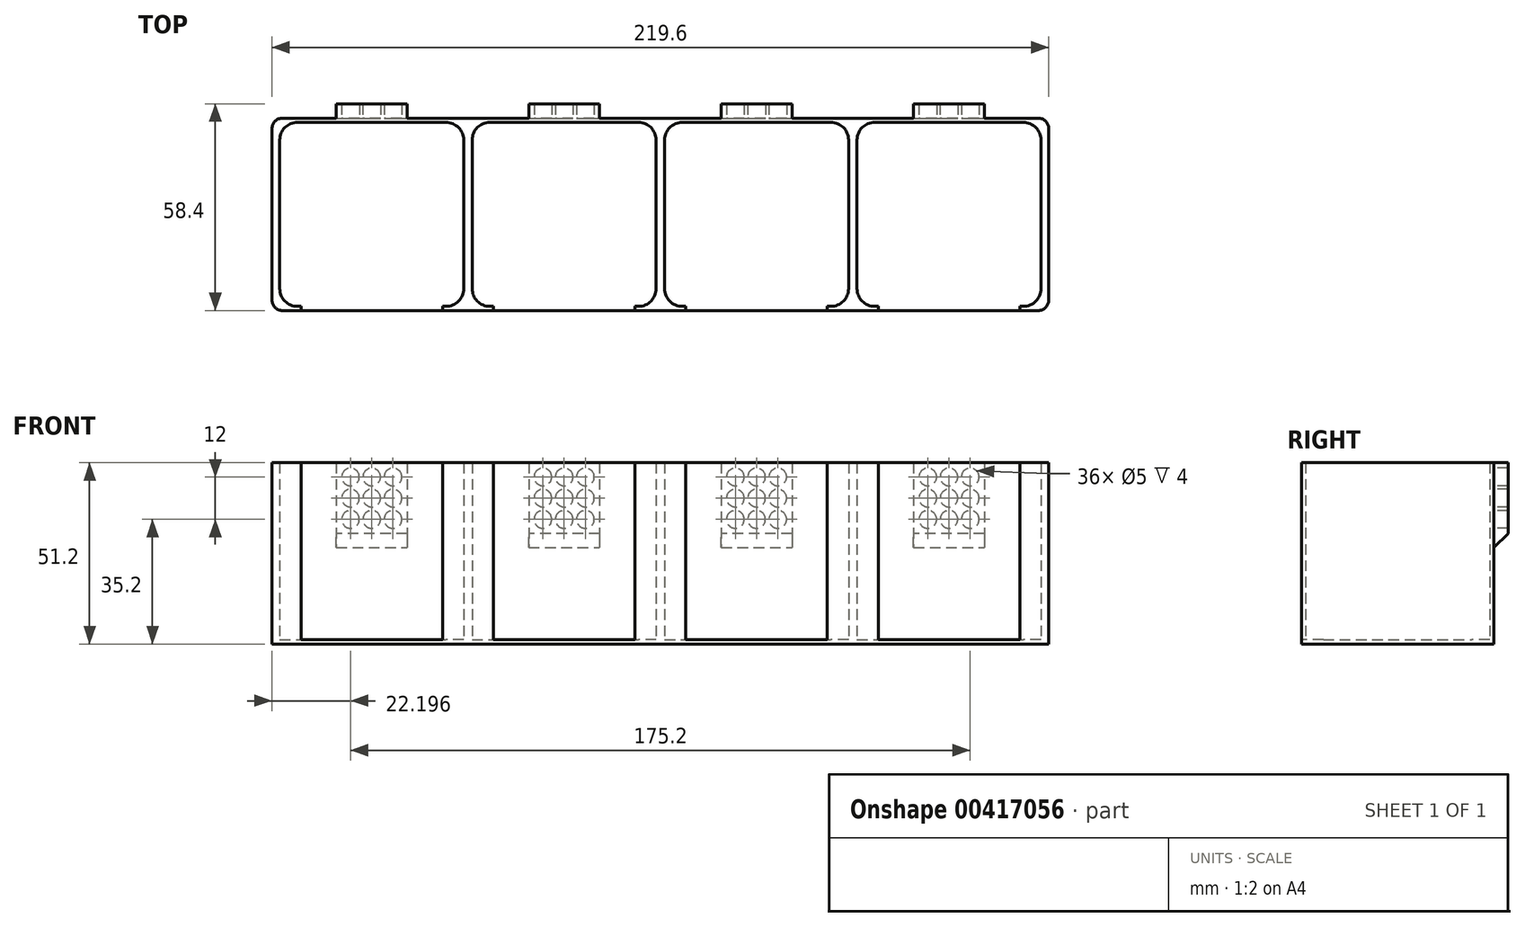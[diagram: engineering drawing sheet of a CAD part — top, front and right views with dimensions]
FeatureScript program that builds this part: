
annotation { "Feature Type Name" : "Feature", "Feature Type Description" : "" }
export const myFeature = defineFeature(function(context is Context, id is Id, definition is map)
    precondition{}
    {
        {
            var Q0;
            Q0=qCreatedBy(makeId("Top.planeOp"),FACE);
            var sketch = newSketch(context, id + "F0", { "sketchPlane" : qUnion([Q0])});
            skLineSegment(sketch, "E0.bottom", {"start": v(-53.6, -9.68) * mm, "end": v(-52.6, -9.68) * mm});
            skLineSegment(sketch, "E0.top", {"start": v(-53.6, 42.32) * mm, "end": v(-11.6, 42.32) * mm});
            skLineSegment(sketch, "E0.left", {"start": v(-58.6, -4.68) * mm, "end": v(-58.6, 37.32) * mm});
            skLineSegment(sketch, "E0.right", {"start": v(-6.6, -4.68) * mm, "end": v(-6.6, 37.32) * mm});
            skCircle(sketch, "E1", {"center": v(-32.6, -9.68) * mm, "radius": 20 * mm, "construction": true});
            skLineSegment(sketch, "E2.trimOffspring", {"start": v(-12.6, -9.68) * mm, "end": v(-11.6, -9.68) * mm});
            skLineSegment(sketch, "E3.0", {"start": v(-12.6, -10.88) * mm, "end": v(-5.4, -10.88) * mm});
            skLineSegment(sketch, "E3.1", {"start": v(-59.8, -10.88) * mm, "end": v(-52.56, -10.88) * mm});
            skLineSegment(sketch, "E3.2", {"start": v(-59.8, -10.88) * mm, "end": v(-59.8, 43.52) * mm});
            skLineSegment(sketch, "E3.3", {"start": v(-59.8, 43.52) * mm, "end": v(-5.4, 43.52) * mm});
            skLineSegment(sketch, "E3.4", {"start": v(-5.4, -10.88) * mm, "end": v(-5.4, 43.52) * mm});
            skLineSegment(sketch, "E4", {"start": v(-52.6, -9.68) * mm, "end": v(-52.6, -10.88) * mm});
            skLineSegment(sketch, "E5", {"start": v(-12.6, -9.68) * mm, "end": v(-12.6, -10.88) * mm});
            skPoint(sketch, "E6.visualSharp", {"position": v(-58.6, 42.32) * mm});
            skArc(sketch, "E6.filletArc", {"start": v(-53.6, 42.32) * mm, "mid": v(-57.13, 40.85) * mm, "end": v(-58.6, 37.32) * mm});
            skPoint(sketch, "E7.visualSharp", {"position": v(-6.6, 42.32) * mm});
            skArc(sketch, "E7.filletArc", {"start": v(-6.6, 37.32) * mm, "mid": v(-8.06, 40.85) * mm, "end": v(-11.6, 42.32) * mm});
            skPoint(sketch, "E8.visualSharp", {"position": v(-58.6, -9.68) * mm});
            skArc(sketch, "E8.filletArc", {"start": v(-58.6, -4.68) * mm, "mid": v(-57.13, -8.22) * mm, "end": v(-53.6, -9.68) * mm});
            skPoint(sketch, "E9.visualSharp", {"position": v(-6.6, -9.68) * mm});
            skArc(sketch, "E9.filletArc", {"start": v(-11.6, -9.68) * mm, "mid": v(-8.06, -8.22) * mm, "end": v(-6.6, -4.68) * mm});
            skPoint(sketch, "E10.1.0.0", {"position": v(-4.2, -9.68) * mm});
            skPoint(sketch, "E10.1.0.1", {"position": v(47.8, 42.32) * mm});
            skPoint(sketch, "E10.1.0.2", {"position": v(-4.2, 42.32) * mm});
            skPoint(sketch, "E10.1.0.3", {"position": v(47.8, -9.68) * mm});
            skLineSegment(sketch, "E10.1.0.4", {"start": v(49, -10.88) * mm, "end": v(49, 43.52) * mm});
            skLineSegment(sketch, "E10.1.0.5", {"start": v(-5.4, 43.52) * mm, "end": v(49, 43.52) * mm});
            skCircle(sketch, "E10.1.0.7", {"center": v(21.8, -9.68) * mm, "radius": 20 * mm, "construction": true});
            skLineSegment(sketch, "E10.1.0.8", {"start": v(-4.2, -4.68) * mm, "end": v(-4.2, 37.32) * mm});
            skLineSegment(sketch, "E10.1.0.9", {"start": v(47.8, -4.68) * mm, "end": v(47.8, 37.32) * mm});
            skLineSegment(sketch, "E10.1.0.10", {"start": v(0.8, 42.32) * mm, "end": v(42.8, 42.32) * mm});
            skArc(sketch, "E10.1.0.11", {"start": v(-4.2, -4.68) * mm, "mid": v(-2.73, -8.22) * mm, "end": v(0.8, -9.68) * mm});
            skArc(sketch, "E10.1.0.12", {"start": v(47.8, 37.32) * mm, "mid": v(46.34, 40.85) * mm, "end": v(42.8, 42.32) * mm});
            skArc(sketch, "E10.1.0.13", {"start": v(0.8, 42.32) * mm, "mid": v(-2.73, 40.85) * mm, "end": v(-4.2, 37.32) * mm});
            skArc(sketch, "E10.1.0.14", {"start": v(42.8, -9.68) * mm, "mid": v(46.34, -8.22) * mm, "end": v(47.8, -4.68) * mm});
            skLineSegment(sketch, "E10.1.0.15", {"start": v(-5.4, -10.88) * mm, "end": v(1.84, -10.88) * mm});
            skLineSegment(sketch, "E10.1.0.16", {"start": v(41.8, -10.88) * mm, "end": v(49, -10.88) * mm});
            skLineSegment(sketch, "E10.1.0.17", {"start": v(0.8, -9.68) * mm, "end": v(1.8, -9.68) * mm});
            skLineSegment(sketch, "E10.1.0.18", {"start": v(41.8, -9.68) * mm, "end": v(41.8, -10.88) * mm});
            skLineSegment(sketch, "E10.1.0.19", {"start": v(1.8, -9.68) * mm, "end": v(1.8, -10.88) * mm});
            skLineSegment(sketch, "E10.1.0.20", {"start": v(41.8, -9.68) * mm, "end": v(42.8, -9.68) * mm});
            skPoint(sketch, "E10.2.0.0", {"position": v(50.2, -9.68) * mm});
            skPoint(sketch, "E10.2.0.1", {"position": v(102.2, 42.32) * mm});
            skPoint(sketch, "E10.2.0.2", {"position": v(50.2, 42.32) * mm});
            skPoint(sketch, "E10.2.0.3", {"position": v(102.2, -9.68) * mm});
            skLineSegment(sketch, "E10.2.0.4", {"start": v(103.4, -10.88) * mm, "end": v(103.4, 43.52) * mm});
            skLineSegment(sketch, "E10.2.0.5", {"start": v(49, 43.52) * mm, "end": v(103.4, 43.52) * mm});
            skLineSegment(sketch, "E10.2.0.6", {"start": v(49, -10.88) * mm, "end": v(49, 43.52) * mm});
            skCircle(sketch, "E10.2.0.7", {"center": v(76.2, -9.68) * mm, "radius": 20 * mm, "construction": true});
            skLineSegment(sketch, "E10.2.0.8", {"start": v(50.2, -4.68) * mm, "end": v(50.2, 37.32) * mm});
            skLineSegment(sketch, "E10.2.0.9", {"start": v(102.2, -4.68) * mm, "end": v(102.2, 37.32) * mm});
            skLineSegment(sketch, "E10.2.0.10", {"start": v(55.2, 42.32) * mm, "end": v(97.2, 42.32) * mm});
            skArc(sketch, "E10.2.0.11", {"start": v(50.2, -4.68) * mm, "mid": v(51.67, -8.22) * mm, "end": v(55.2, -9.68) * mm});
            skArc(sketch, "E10.2.0.12", {"start": v(102.2, 37.32) * mm, "mid": v(100.74, 40.85) * mm, "end": v(97.2, 42.32) * mm});
            skArc(sketch, "E10.2.0.13", {"start": v(55.2, 42.32) * mm, "mid": v(51.67, 40.85) * mm, "end": v(50.2, 37.32) * mm});
            skArc(sketch, "E10.2.0.14", {"start": v(97.2, -9.68) * mm, "mid": v(100.74, -8.22) * mm, "end": v(102.2, -4.68) * mm});
            skLineSegment(sketch, "E10.2.0.15", {"start": v(49, -10.88) * mm, "end": v(56.24, -10.88) * mm});
            skLineSegment(sketch, "E10.2.0.16", {"start": v(96.2, -10.88) * mm, "end": v(103.4, -10.88) * mm});
            skLineSegment(sketch, "E10.2.0.17", {"start": v(55.2, -9.68) * mm, "end": v(56.2, -9.68) * mm});
            skLineSegment(sketch, "E10.2.0.18", {"start": v(96.2, -9.68) * mm, "end": v(96.2, -10.88) * mm});
            skLineSegment(sketch, "E10.2.0.19", {"start": v(56.2, -9.68) * mm, "end": v(56.2, -10.88) * mm});
            skLineSegment(sketch, "E10.2.0.20", {"start": v(96.2, -9.68) * mm, "end": v(97.2, -9.68) * mm});
            skPoint(sketch, "E10.3.0.0", {"position": v(104.6, -9.68) * mm});
            skPoint(sketch, "E10.3.0.1", {"position": v(156.6, 42.32) * mm});
            skPoint(sketch, "E10.3.0.2", {"position": v(104.6, 42.32) * mm});
            skPoint(sketch, "E10.3.0.3", {"position": v(156.6, -9.68) * mm});
            skLineSegment(sketch, "E10.3.0.4", {"start": v(157.8, -10.88) * mm, "end": v(157.8, 43.52) * mm});
            skLineSegment(sketch, "E10.3.0.5", {"start": v(103.4, 43.52) * mm, "end": v(157.8, 43.52) * mm});
            skLineSegment(sketch, "E10.3.0.6", {"start": v(103.4, -10.88) * mm, "end": v(103.4, 43.52) * mm});
            skCircle(sketch, "E10.3.0.7", {"center": v(130.6, -9.68) * mm, "radius": 20 * mm, "construction": true});
            skLineSegment(sketch, "E10.3.0.8", {"start": v(104.6, -4.68) * mm, "end": v(104.6, 37.32) * mm});
            skLineSegment(sketch, "E10.3.0.9", {"start": v(156.6, -4.68) * mm, "end": v(156.6, 37.32) * mm});
            skLineSegment(sketch, "E10.3.0.10", {"start": v(109.6, 42.32) * mm, "end": v(151.6, 42.32) * mm});
            skArc(sketch, "E10.3.0.11", {"start": v(104.6, -4.68) * mm, "mid": v(106.07, -8.22) * mm, "end": v(109.6, -9.68) * mm});
            skArc(sketch, "E10.3.0.12", {"start": v(156.6, 37.32) * mm, "mid": v(155.14, 40.85) * mm, "end": v(151.6, 42.32) * mm});
            skArc(sketch, "E10.3.0.13", {"start": v(109.6, 42.32) * mm, "mid": v(106.07, 40.85) * mm, "end": v(104.6, 37.32) * mm});
            skArc(sketch, "E10.3.0.14", {"start": v(151.6, -9.68) * mm, "mid": v(155.14, -8.22) * mm, "end": v(156.6, -4.68) * mm});
            skLineSegment(sketch, "E10.3.0.15", {"start": v(103.4, -10.88) * mm, "end": v(110.64, -10.88) * mm});
            skLineSegment(sketch, "E10.3.0.16", {"start": v(150.6, -10.88) * mm, "end": v(157.8, -10.88) * mm});
            skLineSegment(sketch, "E10.3.0.17", {"start": v(109.6, -9.68) * mm, "end": v(110.6, -9.68) * mm});
            skLineSegment(sketch, "E10.3.0.18", {"start": v(150.6, -9.68) * mm, "end": v(150.6, -10.88) * mm});
            skLineSegment(sketch, "E10.3.0.19", {"start": v(110.6, -9.68) * mm, "end": v(110.6, -10.88) * mm});
            skLineSegment(sketch, "E10.3.0.20", {"start": v(150.6, -9.68) * mm, "end": v(151.6, -9.68) * mm});
            skLineSegment(sketch, "E10.direction1", {"start": v(-59.8, -10.88) * mm, "end": v(-5.4, -10.88) * mm, "construction": true});
            skLineSegment(sketch, "E11.bottom", {"start": v(-59.8, 43.52) * mm, "end": v(-60.8, 43.52) * mm});
            skLineSegment(sketch, "E11.top", {"start": v(-59.8, -10.88) * mm, "end": v(-60.8, -10.88) * mm});
            skLineSegment(sketch, "E11.left", {"start": v(-59.8, 43.52) * mm, "end": v(-59.8, -10.88) * mm});
            skLineSegment(sketch, "E11.right", {"start": v(-60.8, 43.52) * mm, "end": v(-60.8, -10.88) * mm});
            skLineSegment(sketch, "E12.bottom", {"start": v(157.8, 43.52) * mm, "end": v(158.8, 43.52) * mm});
            skLineSegment(sketch, "E12.top", {"start": v(157.8, -10.88) * mm, "end": v(158.8, -10.88) * mm});
            skLineSegment(sketch, "E12.left", {"start": v(157.8, 43.52) * mm, "end": v(157.8, -10.88) * mm});
            skLineSegment(sketch, "E12.right", {"start": v(158.8, 43.52) * mm, "end": v(158.8, -10.88) * mm});
            skSolve(sketch);
        }
        {
            var Q0;
            Q0 = qSketchRegion(id + "F0", true);
            extrude(context, id + "F1", {"entities" : qUnion([Q0]), "depth" : 50 * mm});
        }
        {
            var Q0;
            Q0=makeQuery(id+"F1.opExtrude","CAP_FACE",FACE,{"disambiguationData":[OSD([sQuery(id+"F0.wireOp",EDGE,"E0.bottom"),sQuery(id+"F0.wireOp",EDGE,"E0.top"),sQuery(id+"F0.wireOp",EDGE,"E0.left"),sQuery(id+"F0.wireOp",EDGE,"E0.right"),sQuery(id+"F0.wireOp",EDGE,"E2.trimOffspring"),sQuery(id+"F0.wireOp",EDGE,"E3.0"),sQuery(id+"F0.wireOp",EDGE,"E3.1"),sQuery(id+"F0.wireOp",EDGE,"E3.2"),sQuery(id+"F0.wireOp",EDGE,"E3.3"),sQuery(id+"F0.wireOp",EDGE,"E4"),sQuery(id+"F0.wireOp",EDGE,"E5"),sQuery(id+"F0.wireOp",EDGE,"E6.filletArc"),sQuery(id+"F0.wireOp",EDGE,"E7.filletArc"),sQuery(id+"F0.wireOp",EDGE,"E8.filletArc"),sQuery(id+"F0.wireOp",EDGE,"E9.filletArc"),sQuery(id+"F0.wireOp",EDGE,"E10.1.0.5"),sQuery(id+"F0.wireOp",EDGE,"E10.1.0.8"),sQuery(id+"F0.wireOp",EDGE,"E10.1.0.9"),sQuery(id+"F0.wireOp",EDGE,"E10.1.0.10"),sQuery(id+"F0.wireOp",EDGE,"E10.1.0.11"),sQuery(id+"F0.wireOp",EDGE,"E10.1.0.12"),sQuery(id+"F0.wireOp",EDGE,"E10.1.0.13"),sQuery(id+"F0.wireOp",EDGE,"E10.1.0.14"),sQuery(id+"F0.wireOp",EDGE,"E10.1.0.15"),sQuery(id+"F0.wireOp",EDGE,"E10.1.0.16"),sQuery(id+"F0.wireOp",EDGE,"E10.1.0.17"),sQuery(id+"F0.wireOp",EDGE,"E10.1.0.18"),sQuery(id+"F0.wireOp",EDGE,"E10.1.0.19"),sQuery(id+"F0.wireOp",EDGE,"E10.1.0.20"),sQuery(id+"F0.wireOp",EDGE,"E10.2.0.5"),sQuery(id+"F0.wireOp",EDGE,"E10.2.0.8"),sQuery(id+"F0.wireOp",EDGE,"E10.2.0.9"),sQuery(id+"F0.wireOp",EDGE,"E10.2.0.10"),sQuery(id+"F0.wireOp",EDGE,"E10.2.0.11"),sQuery(id+"F0.wireOp",EDGE,"E10.2.0.12"),sQuery(id+"F0.wireOp",EDGE,"E10.2.0.13"),sQuery(id+"F0.wireOp",EDGE,"E10.2.0.14"),sQuery(id+"F0.wireOp",EDGE,"E10.2.0.15"),sQuery(id+"F0.wireOp",EDGE,"E10.2.0.16"),sQuery(id+"F0.wireOp",EDGE,"E10.2.0.17"),sQuery(id+"F0.wireOp",EDGE,"E10.2.0.18"),sQuery(id+"F0.wireOp",EDGE,"E10.2.0.19"),sQuery(id+"F0.wireOp",EDGE,"E10.2.0.20"),sQuery(id+"F0.wireOp",EDGE,"E10.3.0.5"),sQuery(id+"F0.wireOp",EDGE,"E10.3.0.8"),sQuery(id+"F0.wireOp",EDGE,"E10.3.0.9"),sQuery(id+"F0.wireOp",EDGE,"E10.3.0.10"),sQuery(id+"F0.wireOp",EDGE,"E10.3.0.11"),sQuery(id+"F0.wireOp",EDGE,"E10.3.0.12"),sQuery(id+"F0.wireOp",EDGE,"E10.3.0.13"),sQuery(id+"F0.wireOp",EDGE,"E10.3.0.14"),sQuery(id+"F0.wireOp",EDGE,"E10.3.0.15"),sQuery(id+"F0.wireOp",EDGE,"E10.3.0.16"),sQuery(id+"F0.wireOp",EDGE,"E10.3.0.17"),sQuery(id+"F0.wireOp",EDGE,"E10.3.0.18"),sQuery(id+"F0.wireOp",EDGE,"E10.3.0.19"),sQuery(id+"F0.wireOp",EDGE,"E10.3.0.20"),sQuery(id+"F0.wireOp",EDGE,"E10.4.0.4"),sQuery(id+"F0.wireOp",EDGE,"E10.4.0.5"),sQuery(id+"F0.wireOp",EDGE,"E10.4.0.8"),sQuery(id+"F0.wireOp",EDGE,"E10.4.0.9"),sQuery(id+"F0.wireOp",EDGE,"E10.4.0.10"),sQuery(id+"F0.wireOp",EDGE,"E10.4.0.11"),sQuery(id+"F0.wireOp",EDGE,"E10.4.0.12"),sQuery(id+"F0.wireOp",EDGE,"E10.4.0.13"),sQuery(id+"F0.wireOp",EDGE,"E10.4.0.14"),sQuery(id+"F0.wireOp",EDGE,"E10.4.0.15"),sQuery(id+"F0.wireOp",EDGE,"E10.4.0.16"),sQuery(id+"F0.wireOp",EDGE,"E10.4.0.17"),sQuery(id+"F0.wireOp",EDGE,"E10.4.0.18"),sQuery(id+"F0.wireOp",EDGE,"E10.4.0.19"),sQuery(id+"F0.wireOp",EDGE,"E10.4.0.20")])],"isStart":true});
            var sketch = newSketch(context, id + "F2", { "sketchPlane" : qUnion([Q0])});
            skLineSegment(sketch, "E13.bottom", {"start": v(-60.8, 10.88) * mm, "end": v(158.8, 10.88) * mm});
            skLineSegment(sketch, "E13.top", {"start": v(-60.8, -43.52) * mm, "end": v(158.8, -43.52) * mm});
            skLineSegment(sketch, "E13.left", {"start": v(-60.8, 10.88) * mm, "end": v(-60.8, -43.52) * mm});
            skLineSegment(sketch, "E13.right", {"start": v(158.8, 10.88) * mm, "end": v(158.8, -43.52) * mm});
            skSolve(sketch);
        }
        {
            var Q0;
            Q0 = qSketchRegion(id + "F2", true);
            extrude(context, id + "F3", {"entities" : qUnion([Q0]), "operationType" : NewBodyOperationType.ADD, "depth" : 1.2 * mm});
        }
        {
            var Q0;
            Q0=makeQuery(id+"F1.opExtrude","SWEPT_FACE",FACE,{"disambiguationData":[OSD([sQuery(id+"F0.wireOp",EDGE,"E0.top")])]});
            var sketch = newSketch(context, id + "F4", { "sketchPlane" : qUnion([Q0])});
            skLineSegment(sketch, "E14.bottom", {"start": v(-22.6, 50) * mm, "end": v(-42.6, 50) * mm});
            skLineSegment(sketch, "E14.top", {"start": v(-22.6, 30) * mm, "end": v(-42.6, 30) * mm});
            skLineSegment(sketch, "E14.left", {"start": v(-22.6, 50) * mm, "end": v(-22.6, 30) * mm});
            skLineSegment(sketch, "E14.right", {"start": v(-42.6, 50) * mm, "end": v(-42.6, 30) * mm});
            skPoint(sketch, "E14.middle", {"position": v(-32.6, 40) * mm});
            skPoint(sketch, "E14.middle.positionSnap0", {"position": v(-32.6, 50) * mm});
            skPoint(sketch, "E14.centerSnap0", {"position": v(-32.6, 50) * mm});
            skCircle(sketch, "E15", {"center": v(-38.6, 34) * mm, "radius": 2.5 * mm});
            skCircle(sketch, "E16.0.1.0", {"center": v(-38.6, 40) * mm, "radius": 2.5 * mm});
            skCircle(sketch, "E16.0.2.0", {"center": v(-38.6, 46) * mm, "radius": 2.5 * mm});
            skCircle(sketch, "E16.1.0.0", {"center": v(-32.6, 34) * mm, "radius": 2.5 * mm});
            skCircle(sketch, "E16.1.1.0", {"center": v(-32.6, 40) * mm, "radius": 2.5 * mm});
            skCircle(sketch, "E16.1.2.0", {"center": v(-32.6, 46) * mm, "radius": 2.5 * mm});
            skCircle(sketch, "E16.2.0.0", {"center": v(-26.6, 34) * mm, "radius": 2.5 * mm});
            skCircle(sketch, "E16.2.1.0", {"center": v(-26.6, 40) * mm, "radius": 2.5 * mm});
            skCircle(sketch, "E16.2.2.0", {"center": v(-26.6, 46) * mm, "radius": 2.5 * mm});
            skLineSegment(sketch, "E16.direction1", {"start": v(-38.6, 34) * mm, "end": v(-32.6, 34) * mm, "construction": true});
            skLineSegment(sketch, "E16.direction2", {"start": v(-38.6, 34) * mm, "end": v(-38.6, 40) * mm, "construction": true});
            skPoint(sketch, "E17.1.0.0", {"position": v(21.8, 50) * mm});
            skCircle(sketch, "E17.1.0.1", {"center": v(27.8, 40) * mm, "radius": 2.5 * mm});
            skCircle(sketch, "E17.1.0.2", {"center": v(15.8, 34) * mm, "radius": 2.5 * mm});
            skCircle(sketch, "E17.1.0.3", {"center": v(21.8, 40) * mm, "radius": 2.5 * mm});
            skCircle(sketch, "E17.1.0.4", {"center": v(15.8, 40) * mm, "radius": 2.5 * mm});
            skCircle(sketch, "E17.1.0.5", {"center": v(27.8, 34) * mm, "radius": 2.5 * mm});
            skPoint(sketch, "E17.1.0.6", {"position": v(21.8, 40) * mm});
            skLineSegment(sketch, "E17.1.0.7", {"start": v(31.8, 30) * mm, "end": v(11.8, 30) * mm});
            skLineSegment(sketch, "E17.1.0.8", {"start": v(31.8, 50) * mm, "end": v(11.8, 50) * mm});
            skLineSegment(sketch, "E17.1.0.9", {"start": v(11.8, 50) * mm, "end": v(11.8, 30) * mm});
            skLineSegment(sketch, "E17.1.0.10", {"start": v(31.8, 50) * mm, "end": v(31.8, 30) * mm});
            skCircle(sketch, "E17.1.0.11", {"center": v(21.8, 34) * mm, "radius": 2.5 * mm});
            skCircle(sketch, "E17.1.0.12", {"center": v(21.8, 46) * mm, "radius": 2.5 * mm});
            skCircle(sketch, "E17.1.0.13", {"center": v(15.8, 46) * mm, "radius": 2.5 * mm});
            skCircle(sketch, "E17.1.0.14", {"center": v(27.8, 46) * mm, "radius": 2.5 * mm});
            skLineSegment(sketch, "E17.1.0.15", {"start": v(15.8, 34) * mm, "end": v(15.8, 40) * mm, "construction": true});
            skLineSegment(sketch, "E17.1.0.16", {"start": v(15.8, 34) * mm, "end": v(21.8, 34) * mm, "construction": true});
            skPoint(sketch, "E17.1.0.17", {"position": v(21.8, 50) * mm});
            skPoint(sketch, "E17.2.0.0", {"position": v(76.2, 50) * mm});
            skCircle(sketch, "E17.2.0.1", {"center": v(82.2, 40) * mm, "radius": 2.5 * mm});
            skCircle(sketch, "E17.2.0.2", {"center": v(70.2, 34) * mm, "radius": 2.5 * mm});
            skCircle(sketch, "E17.2.0.3", {"center": v(76.2, 40) * mm, "radius": 2.5 * mm});
            skCircle(sketch, "E17.2.0.4", {"center": v(70.2, 40) * mm, "radius": 2.5 * mm});
            skCircle(sketch, "E17.2.0.5", {"center": v(82.2, 34) * mm, "radius": 2.5 * mm});
            skPoint(sketch, "E17.2.0.6", {"position": v(76.2, 40) * mm});
            skLineSegment(sketch, "E17.2.0.7", {"start": v(86.2, 30) * mm, "end": v(66.2, 30) * mm});
            skLineSegment(sketch, "E17.2.0.8", {"start": v(86.2, 50) * mm, "end": v(66.2, 50) * mm});
            skLineSegment(sketch, "E17.2.0.9", {"start": v(66.2, 50) * mm, "end": v(66.2, 30) * mm});
            skLineSegment(sketch, "E17.2.0.10", {"start": v(86.2, 50) * mm, "end": v(86.2, 30) * mm});
            skCircle(sketch, "E17.2.0.11", {"center": v(76.2, 34) * mm, "radius": 2.5 * mm});
            skCircle(sketch, "E17.2.0.12", {"center": v(76.2, 46) * mm, "radius": 2.5 * mm});
            skCircle(sketch, "E17.2.0.13", {"center": v(70.2, 46) * mm, "radius": 2.5 * mm});
            skCircle(sketch, "E17.2.0.14", {"center": v(82.2, 46) * mm, "radius": 2.5 * mm});
            skLineSegment(sketch, "E17.2.0.15", {"start": v(70.2, 34) * mm, "end": v(70.2, 40) * mm, "construction": true});
            skLineSegment(sketch, "E17.2.0.16", {"start": v(70.2, 34) * mm, "end": v(76.2, 34) * mm, "construction": true});
            skPoint(sketch, "E17.2.0.17", {"position": v(76.2, 50) * mm});
            skPoint(sketch, "E17.3.0.0", {"position": v(130.6, 50) * mm});
            skCircle(sketch, "E17.3.0.1", {"center": v(136.6, 40) * mm, "radius": 2.5 * mm});
            skCircle(sketch, "E17.3.0.2", {"center": v(124.6, 34) * mm, "radius": 2.5 * mm});
            skCircle(sketch, "E17.3.0.3", {"center": v(130.6, 40) * mm, "radius": 2.5 * mm});
            skCircle(sketch, "E17.3.0.4", {"center": v(124.6, 40) * mm, "radius": 2.5 * mm});
            skCircle(sketch, "E17.3.0.5", {"center": v(136.6, 34) * mm, "radius": 2.5 * mm});
            skPoint(sketch, "E17.3.0.6", {"position": v(130.6, 40) * mm});
            skLineSegment(sketch, "E17.3.0.7", {"start": v(140.6, 30) * mm, "end": v(120.6, 30) * mm});
            skLineSegment(sketch, "E17.3.0.8", {"start": v(140.6, 50) * mm, "end": v(120.6, 50) * mm});
            skLineSegment(sketch, "E17.3.0.9", {"start": v(120.6, 50) * mm, "end": v(120.6, 30) * mm});
            skLineSegment(sketch, "E17.3.0.10", {"start": v(140.6, 50) * mm, "end": v(140.6, 30) * mm});
            skCircle(sketch, "E17.3.0.11", {"center": v(130.6, 34) * mm, "radius": 2.5 * mm});
            skCircle(sketch, "E17.3.0.12", {"center": v(130.6, 46) * mm, "radius": 2.5 * mm});
            skCircle(sketch, "E17.3.0.13", {"center": v(124.6, 46) * mm, "radius": 2.5 * mm});
            skCircle(sketch, "E17.3.0.14", {"center": v(136.6, 46) * mm, "radius": 2.5 * mm});
            skLineSegment(sketch, "E17.3.0.15", {"start": v(124.6, 34) * mm, "end": v(124.6, 40) * mm, "construction": true});
            skLineSegment(sketch, "E17.3.0.16", {"start": v(124.6, 34) * mm, "end": v(130.6, 34) * mm, "construction": true});
            skPoint(sketch, "E17.3.0.17", {"position": v(130.6, 50) * mm});
            skLineSegment(sketch, "E17.direction1", {"start": v(-42.6, 30) * mm, "end": v(11.8, 30) * mm, "construction": true});
            skSolve(sketch);
        }
        {
            var Q0;
            Q0 = qSketchRegion(id + "F4", true);
            extrude(context, id + "F5", {"entities" : qUnion([Q0]), "operationType" : NewBodyOperationType.ADD, "oppositeDirection" : true, "depth" : 5.2 * mm});
        }
        {
            var Q0;
            Q0=makeQuery(id+"F3.boolean.opBoolean","MERGE",EDGE,{"derivedFrom":[makeQuery(id+"F1.opExtrude","SWEPT_EDGE",EDGE,{"disambiguationData":[OSD([sQuery(id+"F0.wireOp",EDGE,"E11.top"),sQuery(id+"F0.wireOp",EDGE,"E11.right")])]}),makeQuery(id+"F3.opExtrude","SWEPT_EDGE",EDGE,{"disambiguationData":[OSD([sQuery(id+"F2.wireOp",EDGE,"E13.bottom"),sQuery(id+"F2.wireOp",EDGE,"E13.left")])]})]});
            var Q1;
            Q1=makeQuery(id+"F3.boolean.opBoolean","MERGE",EDGE,{"derivedFrom":[makeQuery(id+"F1.opExtrude","SWEPT_EDGE",EDGE,{"disambiguationData":[OSD([sQuery(id+"F0.wireOp",EDGE,"E12.top"),sQuery(id+"F0.wireOp",EDGE,"E12.right")])]}),makeQuery(id+"F3.opExtrude","SWEPT_EDGE",EDGE,{"disambiguationData":[OSD([sQuery(id+"F2.wireOp",EDGE,"E13.bottom"),sQuery(id+"F2.wireOp",EDGE,"E13.right")])]})]});
            var Q2;
            Q2=makeQuery(id+"F3.boolean.opBoolean","MERGE",EDGE,{"derivedFrom":[makeQuery(id+"F1.opExtrude","SWEPT_EDGE",EDGE,{"disambiguationData":[OSD([sQuery(id+"F0.wireOp",EDGE,"E11.bottom"),sQuery(id+"F0.wireOp",EDGE,"E11.right")])]}),makeQuery(id+"F3.opExtrude","SWEPT_EDGE",EDGE,{"disambiguationData":[OSD([sQuery(id+"F2.wireOp",EDGE,"E13.top"),sQuery(id+"F2.wireOp",EDGE,"E13.left")])]})]});
            var Q3;
            Q3=makeQuery(id+"F3.boolean.opBoolean","MERGE",EDGE,{"derivedFrom":[makeQuery(id+"F1.opExtrude","SWEPT_EDGE",EDGE,{"disambiguationData":[OSD([sQuery(id+"F0.wireOp",EDGE,"E12.bottom"),sQuery(id+"F0.wireOp",EDGE,"E12.right")])]}),makeQuery(id+"F3.opExtrude","SWEPT_EDGE",EDGE,{"disambiguationData":[OSD([sQuery(id+"F2.wireOp",EDGE,"E13.top"),sQuery(id+"F2.wireOp",EDGE,"E13.right")])]})]});
            fillet(context, id + "F6", {"entities" : qUnion([Q0, Q1, Q2, Q3]), "radius" : 3 * mm, "tangentPropagation" : true, "allowEdgeOverflow" : false});
        }
        {
            var Q0;
            Q0=makeQuery(id+"F5.boolean.opBoolean","INTERSECT",EDGE,{"derivedFrom":[makeQuery(id+"F3.boolean.opBoolean","MERGE",FACE,{"derivedFrom":[makeQuery(id+"F1.opExtrude","SWEPT_FACE",FACE,{"disambiguationData":[OSD([sQuery(id+"F0.wireOp",EDGE,"E3.3"),sQuery(id+"F0.wireOp",EDGE,"E10.1.0.5"),sQuery(id+"F0.wireOp",EDGE,"E10.2.0.5"),sQuery(id+"F0.wireOp",EDGE,"E10.3.0.5"),sQuery(id+"F0.wireOp",EDGE,"E11.bottom"),sQuery(id+"F0.wireOp",EDGE,"E12.bottom")])]}),makeQuery(id+"F3.opExtrude","SWEPT_FACE",FACE,{"disambiguationData":[OSD([sQuery(id+"F2.wireOp",EDGE,"E13.top")])]})]}),makeQuery(id+"F5.opExtrude","SWEPT_FACE",FACE,{"disambiguationData":[OSD([sQuery(id+"F4.wireOp",EDGE,"E17.3.0.7")])]})]});
            var Q1;
            Q1=makeQuery(id+"F5.boolean.opBoolean","INTERSECT",EDGE,{"derivedFrom":[makeQuery(id+"F3.boolean.opBoolean","MERGE",FACE,{"derivedFrom":[makeQuery(id+"F1.opExtrude","SWEPT_FACE",FACE,{"disambiguationData":[OSD([sQuery(id+"F0.wireOp",EDGE,"E3.3"),sQuery(id+"F0.wireOp",EDGE,"E10.1.0.5"),sQuery(id+"F0.wireOp",EDGE,"E10.2.0.5"),sQuery(id+"F0.wireOp",EDGE,"E10.3.0.5"),sQuery(id+"F0.wireOp",EDGE,"E11.bottom"),sQuery(id+"F0.wireOp",EDGE,"E12.bottom")])]}),makeQuery(id+"F3.opExtrude","SWEPT_FACE",FACE,{"disambiguationData":[OSD([sQuery(id+"F2.wireOp",EDGE,"E13.top")])]})]}),makeQuery(id+"F5.opExtrude","SWEPT_FACE",FACE,{"disambiguationData":[OSD([sQuery(id+"F4.wireOp",EDGE,"E17.2.0.7")])]})]});
            var Q2;
            Q2=makeQuery(id+"F5.boolean.opBoolean","INTERSECT",EDGE,{"derivedFrom":[makeQuery(id+"F3.boolean.opBoolean","MERGE",FACE,{"derivedFrom":[makeQuery(id+"F1.opExtrude","SWEPT_FACE",FACE,{"disambiguationData":[OSD([sQuery(id+"F0.wireOp",EDGE,"E3.3"),sQuery(id+"F0.wireOp",EDGE,"E10.1.0.5"),sQuery(id+"F0.wireOp",EDGE,"E10.2.0.5"),sQuery(id+"F0.wireOp",EDGE,"E10.3.0.5"),sQuery(id+"F0.wireOp",EDGE,"E11.bottom"),sQuery(id+"F0.wireOp",EDGE,"E12.bottom")])]}),makeQuery(id+"F3.opExtrude","SWEPT_FACE",FACE,{"disambiguationData":[OSD([sQuery(id+"F2.wireOp",EDGE,"E13.top")])]})]}),makeQuery(id+"F5.opExtrude","SWEPT_FACE",FACE,{"disambiguationData":[OSD([sQuery(id+"F4.wireOp",EDGE,"E17.1.0.7")])]})]});
            var Q3;
            Q3=makeQuery(id+"F5.boolean.opBoolean","INTERSECT",EDGE,{"derivedFrom":[makeQuery(id+"F3.boolean.opBoolean","MERGE",FACE,{"derivedFrom":[makeQuery(id+"F1.opExtrude","SWEPT_FACE",FACE,{"disambiguationData":[OSD([sQuery(id+"F0.wireOp",EDGE,"E3.3"),sQuery(id+"F0.wireOp",EDGE,"E10.1.0.5"),sQuery(id+"F0.wireOp",EDGE,"E10.2.0.5"),sQuery(id+"F0.wireOp",EDGE,"E10.3.0.5"),sQuery(id+"F0.wireOp",EDGE,"E11.bottom"),sQuery(id+"F0.wireOp",EDGE,"E12.bottom")])]}),makeQuery(id+"F3.opExtrude","SWEPT_FACE",FACE,{"disambiguationData":[OSD([sQuery(id+"F2.wireOp",EDGE,"E13.top")])]})]}),makeQuery(id+"F5.opExtrude","SWEPT_FACE",FACE,{"disambiguationData":[OSD([sQuery(id+"F4.wireOp",EDGE,"E14.top")])]})]});
            chamfer(context, id + "F7", {"entities" : qUnion([Q0, Q1, Q2, Q3]), "width" : 4 * mm, "tangentPropagation" : true});
        }
    });
